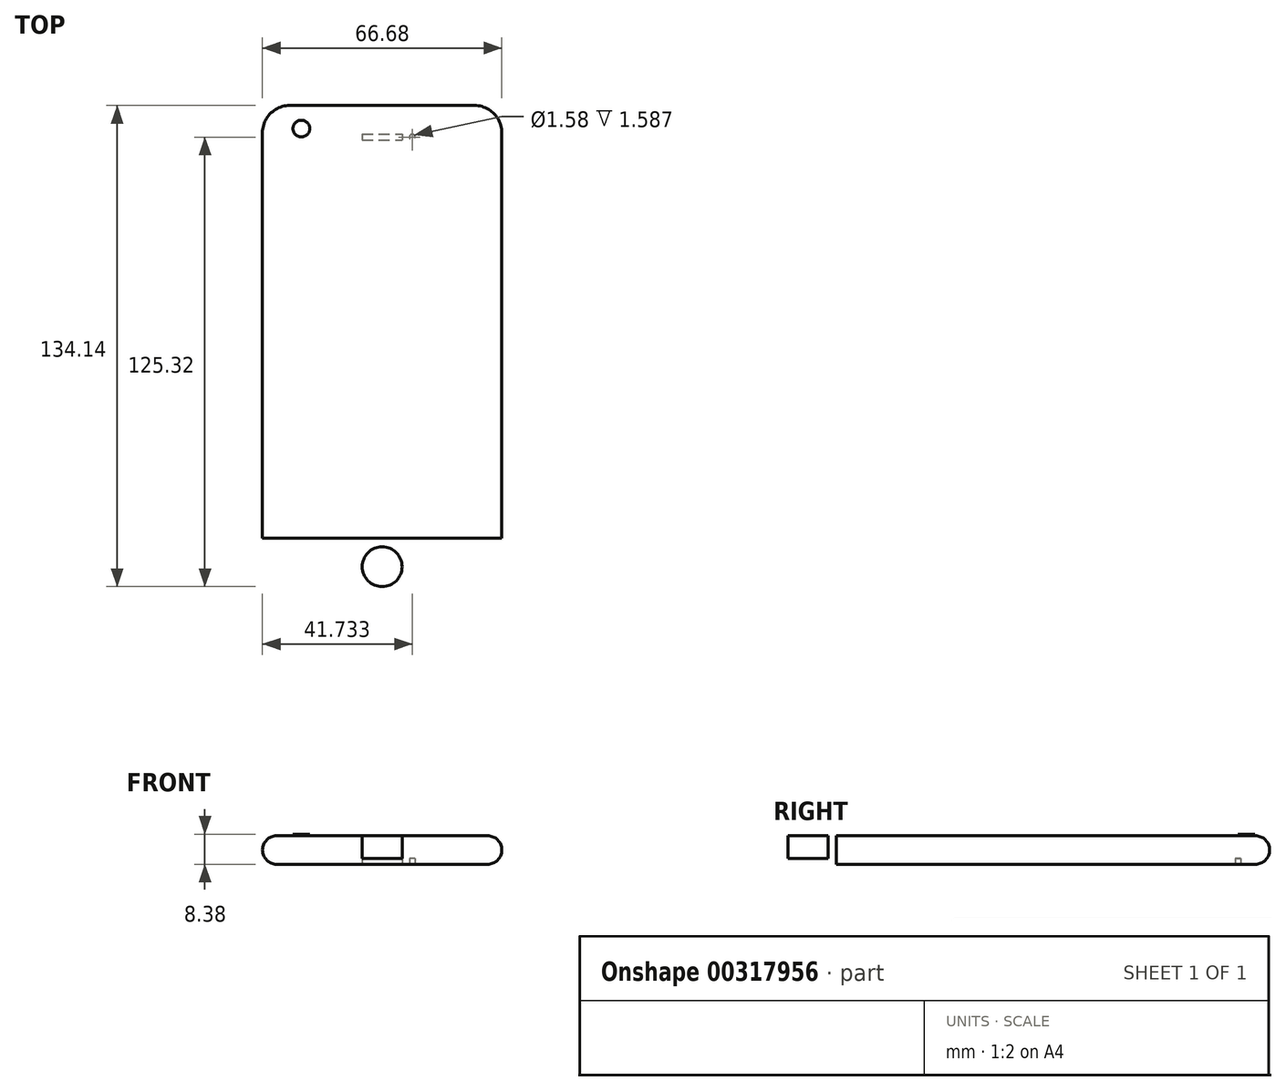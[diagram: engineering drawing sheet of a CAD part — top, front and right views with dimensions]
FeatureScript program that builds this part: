
annotation { "Feature Type Name" : "Feature", "Feature Type Description" : "" }
export const myFeature = defineFeature(function(context is Context, id is Id, definition is map)
    precondition{}
    {
        {
            var Q0;
            Q0=qCreatedBy(makeId("Top.planeOp"),FACE);
            var sketch = newSketch(context, id + "F0", { "sketchPlane" : qUnion([Q0])});
            skLineSegment(sketch, "E0.bottom", {"start": v(33.34, -68.26) * mm, "end": v(-33.34, -68.26) * mm});
            skLineSegment(sketch, "E0.top", {"start": v(33.34, 68.26) * mm, "end": v(-33.34, 68.26) * mm});
            skLineSegment(sketch, "E0.left", {"start": v(33.34, -68.26) * mm, "end": v(33.34, 68.26) * mm});
            skLineSegment(sketch, "E0.right", {"start": v(-33.34, -68.26) * mm, "end": v(-33.34, 68.26) * mm});
            skPoint(sketch, "E0.middle", {"position": v(0, 0) * mm});
            skLineSegment(sketch, "E1.bottom", {"start": v(-33.34, -68.26) * mm, "end": v(33.34, -68.26) * mm});
            skLineSegment(sketch, "E1.top", {"start": v(-33.34, -52.39) * mm, "end": v(33.34, -52.39) * mm});
            skLineSegment(sketch, "E1.left", {"start": v(-33.34, -68.26) * mm, "end": v(-33.34, -52.39) * mm});
            skLineSegment(sketch, "E1.right", {"start": v(33.34, -68.26) * mm, "end": v(33.34, -52.39) * mm});
            skCircle(sketch, "E2", {"center": v(0, -60.33) * mm, "radius": 5.56 * mm});
            skPoint(sketch, "E2.centerSnap0", {"position": v(33.34, -60.33) * mm});
            skPoint(sketch, "E2.centerSnap1", {"position": v(0, -68.26) * mm});
            skLineSegment(sketch, "E3.bottom", {"start": v(5.56, 58.65) * mm, "end": v(-5.56, 58.65) * mm});
            skLineSegment(sketch, "E3.top", {"start": v(5.56, 60.24) * mm, "end": v(-5.56, 60.24) * mm});
            skLineSegment(sketch, "E3.left", {"start": v(5.56, 58.65) * mm, "end": v(5.56, 60.24) * mm});
            skLineSegment(sketch, "E3.right", {"start": v(-5.56, 58.65) * mm, "end": v(-5.56, 60.24) * mm});
            skPoint(sketch, "E3.middle", {"position": v(0, 59.44) * mm});
            skCircle(sketch, "E4", {"center": v(-8.45, 59.44) * mm, "radius": 0.8 * mm});
            skPoint(sketch, "E4.centerSnap0", {"position": v(-5.56, 59.44) * mm});
            skSolve(sketch);
        }
        {
            var Q0;
            Q0=makeQuery(id+"F0.imprint","IMPRINT",FACE,{"disambiguationData":[TD([[makeQuery(id+"F0.imprint","IMPRINT",EDGE,{"derivedFrom":sQuery(id+"F0.wireOp",EDGE,"E1.bottom")}),1.0]])]});
            var Q1;
            Q1=makeQuery(id+"F0.imprint","IMPRINT",FACE,{"disambiguationData":[TD([[makeQuery(id+"F0.imprint","IMPRINT",EDGE,{"derivedFrom":sQuery(id+"F0.wireOp",EDGE,"E2")}),1.0]])]});
            var Q2;
            Q2=makeQuery(id+"F0.imprint","IMPRINT",FACE,{"disambiguationData":[TD([[makeQuery(id+"F0.imprint","IMPRINT",EDGE,{"derivedFrom":sQuery(id+"F0.wireOp",EDGE,"E3.bottom")}),-1.0]])]});
            var Q3;
            Q3=makeQuery(id+"F0.imprint","IMPRINT",FACE,{"disambiguationData":[TD([[makeQuery(id+"F0.imprint","IMPRINT",EDGE,{"derivedFrom":sQuery(id+"F0.wireOp",EDGE,"E0.top")}),1.0]])]});
            var Q4;
            Q4=makeQuery(id+"F0.imprint","IMPRINT",FACE,{"disambiguationData":[TD([[makeQuery(id+"F0.imprint","IMPRINT",EDGE,{"derivedFrom":sQuery(id+"F0.wireOp",EDGE,"E4")}),1.0]])]});
            extrude(context, id + "F1", {"entities" : qUnion([Q0, Q1, Q2, Q3, Q4]), "depth" : 7.94 * mm});
        }
        {
            var Q0;
            Q0=qCreatedBy(makeId("Top.planeOp"),FACE);
            var sketch = newSketch(context, id + "F2", { "sketchPlane" : qUnion([Q0])});
            skPoint(sketch, "E5.middle", {"position": v(0, 59.47) * mm});
            skLineSegment(sketch, "E6.bottom", {"start": v(-5.55, 60.23) * mm, "end": v(5.55, 60.23) * mm});
            skLineSegment(sketch, "E6.top", {"start": v(-5.55, 58.65) * mm, "end": v(5.55, 58.65) * mm});
            skLineSegment(sketch, "E6.left", {"start": v(-5.55, 60.23) * mm, "end": v(-5.55, 58.65) * mm});
            skLineSegment(sketch, "E6.right", {"start": v(5.55, 60.23) * mm, "end": v(5.55, 58.65) * mm});
            skCircle(sketch, "E7", {"center": v(8.4, 59.44) * mm, "radius": 0.79 * mm});
            skPoint(sketch, "E7.centerSnap0", {"position": v(5.55, 59.44) * mm});
            skSolve(sketch);
        }
        {
            var Q0;
            Q0 = qSketchRegion(id + "F2", true);
            extrude(context, id + "F3", {"entities" : qUnion([Q0]), "operationType" : NewBodyOperationType.REMOVE, "depth" : 1.59 * mm});
        }
        {
            var Q0;
            Q0=makeQuery(id+"F0.imprint","IMPRINT",FACE,{"disambiguationData":[TD([[makeQuery(id+"F0.imprint","IMPRINT",EDGE,{"derivedFrom":sQuery(id+"F0.wireOp",EDGE,"E2")}),1.0]])]});
            extrude(context, id + "F4", {"entities" : qUnion([Q0]), "operationType" : NewBodyOperationType.REMOVE, "depth" : 1.59 * mm});
        }
        {
            var Q0;
            Q0=makeQuery(id+"F1.opExtrude","SWEPT_EDGE",EDGE,{"disambiguationData":[OSD([sQuery(id+"F0.wireOp",EDGE,"E0.top"),sQuery(id+"F0.wireOp",EDGE,"E0.right")])]});
            var Q1;
            Q1=makeQuery(id+"F1.opExtrude","SWEPT_EDGE",EDGE,{"disambiguationData":[OSD([sQuery(id+"F0.wireOp",EDGE,"E0.top"),sQuery(id+"F0.wireOp",EDGE,"E0.left")])]});
            var Q2;
            Q2=makeQuery(id+"F1.opExtrude","SWEPT_EDGE",EDGE,{"disambiguationData":[OSD([sQuery(id+"F0.wireOp",EDGE,"E1.bottom"),sQuery(id+"F0.wireOp",EDGE,"E1.right")])]});
            var Q3;
            Q3=makeQuery(id+"F1.opExtrude","SWEPT_EDGE",EDGE,{"disambiguationData":[OSD([sQuery(id+"F0.wireOp",EDGE,"E1.bottom"),sQuery(id+"F0.wireOp",EDGE,"E1.left")])]});
            fillet(context, id + "F5", {"entities" : qUnion([Q0, Q1, Q2, Q3]), "radius" : 7.62 * mm, "tangentPropagation" : true, "allowEdgeOverflow" : false});
        }
        {
            var Q0;
            Q0=makeQuery(id+"F1.opExtrude","CAP_EDGE",EDGE,{"disambiguationData":[OSD([sQuery(id+"F0.wireOp",EDGE,"E0.left"),sQuery(id+"F0.wireOp",EDGE,"E1.right")])],"isStart":true});
            var Q1;
            Q1=makeQuery(id+"F1.opExtrude","CAP_EDGE",EDGE,{"disambiguationData":[OSD([sQuery(id+"F0.wireOp",EDGE,"E0.left"),sQuery(id+"F0.wireOp",EDGE,"E1.right")])],"isStart":false});
            fillet(context, id + "F6", {"entities" : qUnion([Q0, Q1]), "radius" : 3.97 * mm, "tangentPropagation" : true, "allowEdgeOverflow" : false});
        }
        {
            var Q0;
            Q0=makeQuery(id+"F0.imprint","IMPRINT",FACE,{"disambiguationData":[TD([[makeQuery(id+"F0.imprint","IMPRINT",EDGE,{"derivedFrom":sQuery(id+"F0.wireOp",EDGE,"E0.top")}),1.0]])]});
            var sketch = newSketch(context, id + "F7", { "sketchPlane" : qUnion([Q0])});
            skCircle(sketch, "E8", {"center": v(-22.51, 61.81) * mm, "radius": 2.33 * mm});
            skSolve(sketch);
        }
        {
            var Q0;
            Q0 = qSketchRegion(id + "F7", true);
            extrude(context, id + "F8", {"entities" : qUnion([Q0]), "operationType" : NewBodyOperationType.ADD, "depth" : 8.38 * mm});
        }
    });
